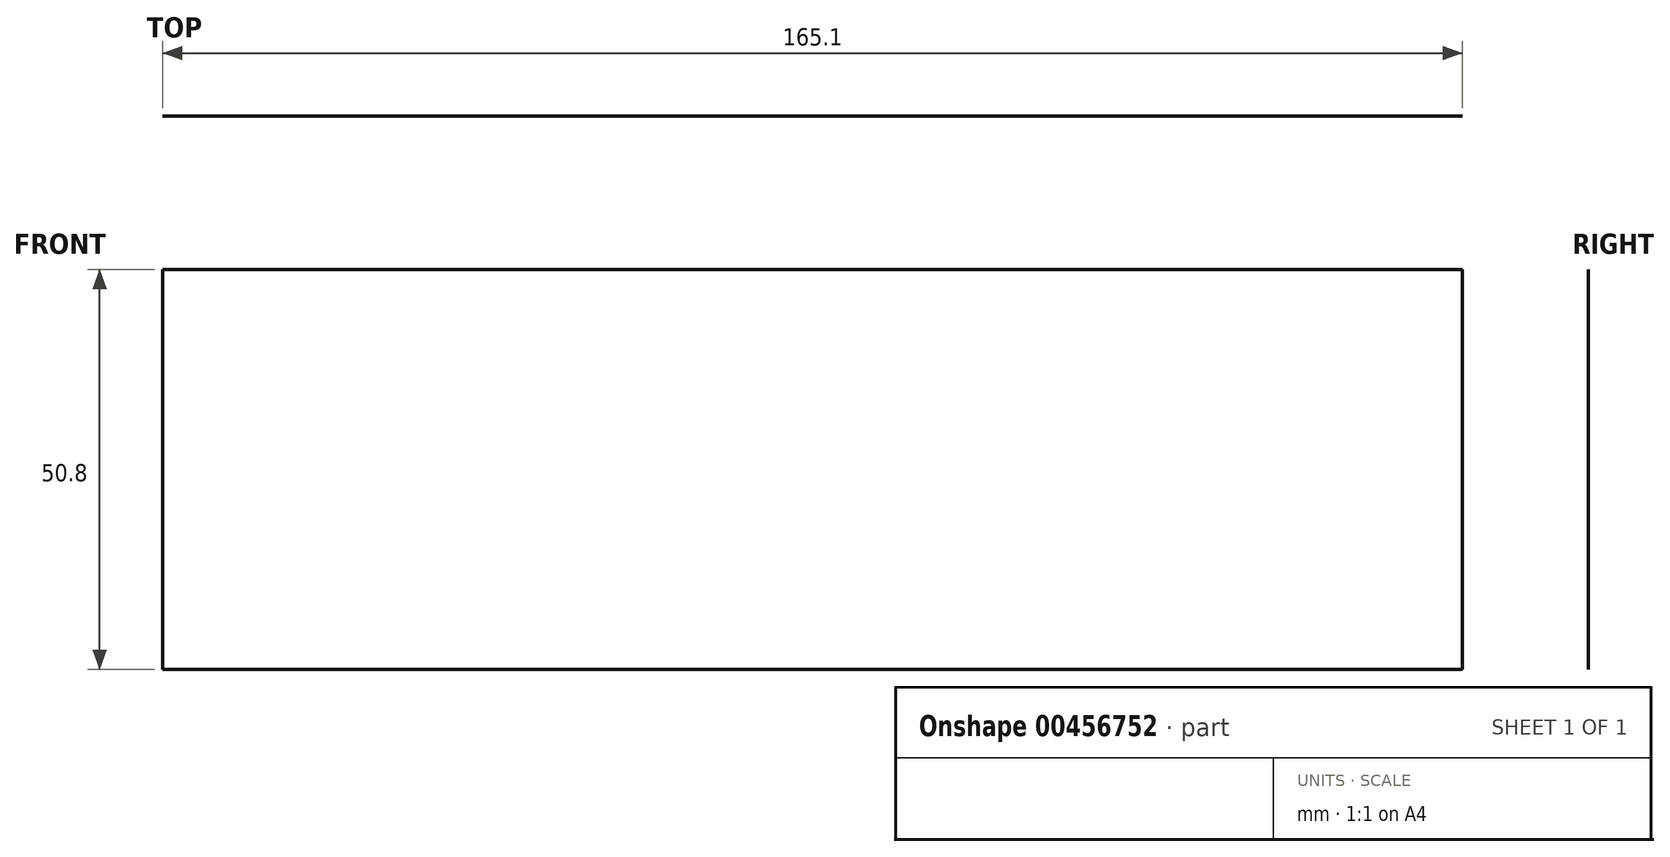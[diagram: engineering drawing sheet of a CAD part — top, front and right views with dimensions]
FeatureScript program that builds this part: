
annotation { "Feature Type Name" : "Feature", "Feature Type Description" : "" }
export const myFeature = defineFeature(function(context is Context, id is Id, definition is map)
    precondition{}
    {
        {
            var Q0;
            Q0=qCreatedBy(makeId("Front.planeOp"),FACE);
            var sketch = newSketch(context, id + "F0", { "sketchPlane" : qUnion([Q0])});
            skLineSegment(sketch, "E0.bottom", {"start": v(0, 0) * mm, "end": v(-165.1, 0) * mm});
            skLineSegment(sketch, "E0.top", {"start": v(0, 50.8) * mm, "end": v(-165.1, 50.8) * mm});
            skLineSegment(sketch, "E0.left", {"start": v(0, 0) * mm, "end": v(0, 50.8) * mm});
            skLineSegment(sketch, "E0.right", {"start": v(-165.1, 0) * mm, "end": v(-165.1, 50.8) * mm});
            skSolve(sketch);
        }
        {
            var Q0;
            Q0=makeQuery(id+"F0.imprint","IMPRINT",FACE,{"disambiguationData":[TD([[makeQuery(id+"F0.imprint","IMPRINT",EDGE,{"derivedFrom":sQuery(id+"F0.wireOp",EDGE,"E0.bottom")}),-1.0]])]});
            extrude(context, id + "F1", {"entities" : qUnion([Q0]), "depth" : 1 / 203.2 * mm});
        }
    });
